# Revit family: powerbrik_r__slim_gen_2_51fc207a410as_10a0
name_source: partatom
category: Lighting Fixtures
units: mm (PartAtom-declared; Revit-internal decimal feet)

## family parameters
Cut with Voids When Loaded = No
Host = Face
Light Source = No
Part Type = Normal
Room Calculation Point = No
Round Connector Dimension = Use Diameter
Shared = No

## types (1)
- POWERBRIK® Slim Gen.2 (1 x LED, 900 lm, 6.5 W, 4000K)
    Apparent Load = 7 VA
    CIE Flux Codes = 43 73 91 87 100
    Color Rendering = 80
    Color Temperature = 4000K
    Default Elevation = 1800 mm
    Description = POWERBRIK® Slim Gen.2, damp-proof luminaire, primary optical cover: enclosure, of PC, primary light characteristic: asymmetric, installation type: surface-mounted, LED, rated luminous flux: 900lm, luminous efficacy: 139lm/W, light colour: 840, colour temperature: 4000K, control gear: ON/OFF, with terminal, 2-pole, max. 1.5mm², mains connection: 230V, AC/DC, 0/50..60Hz, rated input power: 6.5W, housing, of PC, traffic white (RAL 9016), length: 350mm, width: 35mm, height: 22mm, protection rating (complete): IP65, insulation class (complete): insulation class II (safety insulation), certification: CE, UKCA, protection symbol: D, impact resistance: IK05, permissible operating ambient temperature: -20..+40°C, standard: EN 60598-2-1, corresponds to IFS (International Featured Standards) requirements for safety and quality in the food industry, unprotected outdoor installations, contact your sales advisor before using the luminaires in applications with unclear chemical exposure, large temperature fluctuations or condensation-forming humidity, packaging unit: 1 piece
    Height = 42 mm
    Lamp = 1 x LED
    Lamp Light Flux = 900 lm
    Lamp Power = 6.5 W
    Lamp count = 1
    Length = 349 mm
    Luminous efficacy = 138 lm/W
    Manufacturer = Siteco
    ModVariant = No
    Model = 51FC207A410AS
    Mounting Place = Ceiling
    Mounting Type = Surface mounted
    Number of Poles = 1
    OnlyDefault = Yes
    Power Factor = 1
    Product Name = POWERBRIK® Slim Gen.2
    Product group = damp-proof luminaire
    ProductGroupID = 301
    Protection Class = Protection class II
    Protection Degree = IP 65
    RLX_Detail_Level = 1
    RLX_Emergency_Light_Flux = 0 lm
    RLX_Emergency_Type = 0
    RLX_Emergency_Type_DB = No
    RlxData = <blob elided: 49841 chars, md5=51642070>
    Socket = socket
    Standby Power = 0 W
    System Light Flux = 900 lm
    System Power = 7 W
    Type Comments = Product without accessories
    Type Image = l_1331199.jpg
    URL = http://relux.com
    VarID = ---
    Voltage = 0 V
    Weight = 0.00 kg
    Width = 35 mm

## geometry (parser evidence)
native form markers: Sweep x14
no freeform markers — native parametric forms only
